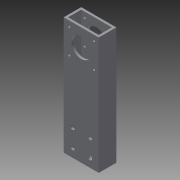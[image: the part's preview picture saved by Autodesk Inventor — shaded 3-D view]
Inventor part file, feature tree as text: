
AUTODESK INVENTOR PART (.ipt)
format: ipt  version: 2013 (Build 170138000, 138)  size: 135,680 bytes
history: native  units: in
note: dims shown in document units (in); Inventor stores cm internally (conversion verified against a paired STEP export)
features: extrude x3, sketch x3
ambient origin geometry x8: Origin, YZ Plane, XZ Plane, XY Plane, X Axis, Y Axis, Z Axis, Center Point
bodies: Solid1 (feature_tree)
feature tree (6):
  extrude  "Extrusion1"  Depth=6.688in
  extrude  "Extrusion2"  TaperAngle=90.0deg  [1 undecoded]
  extrude  "Extrusion3"  Depth=1.0in
  sketch  "Sketch1"  dims[d0=2.0in d1=6.688in]
  sketch  "Sketch2"  dims[d2=1.0in d3=90.0deg]
  sketch  "Sketch3"  dims[d4=1.125in d5=1.0in d6=45.0deg d7=2.0in d9=0.16in d10=0.16in d11=0.16in d12=0.16in d13=2.0in d14=1.5in d15=0.5in d16=180.0deg d17=1.0in d18=0.0in d19=0.25in d20=0.25in d21=1.0in d22=0.0in d23=0.125in d24=0.125in d25=1.75in d26=0.75in d27=10.0in d28=0.0in d29=1.0in d30=1.0in d31=0.25in d32=0.25in d33=1.0in d34=0.0in]
note: 1 required parameter value undecoded (feature->parameter linkage not recoverable at this tier; creation-order binding heuristic only, values carry confidence <= 0.55)
